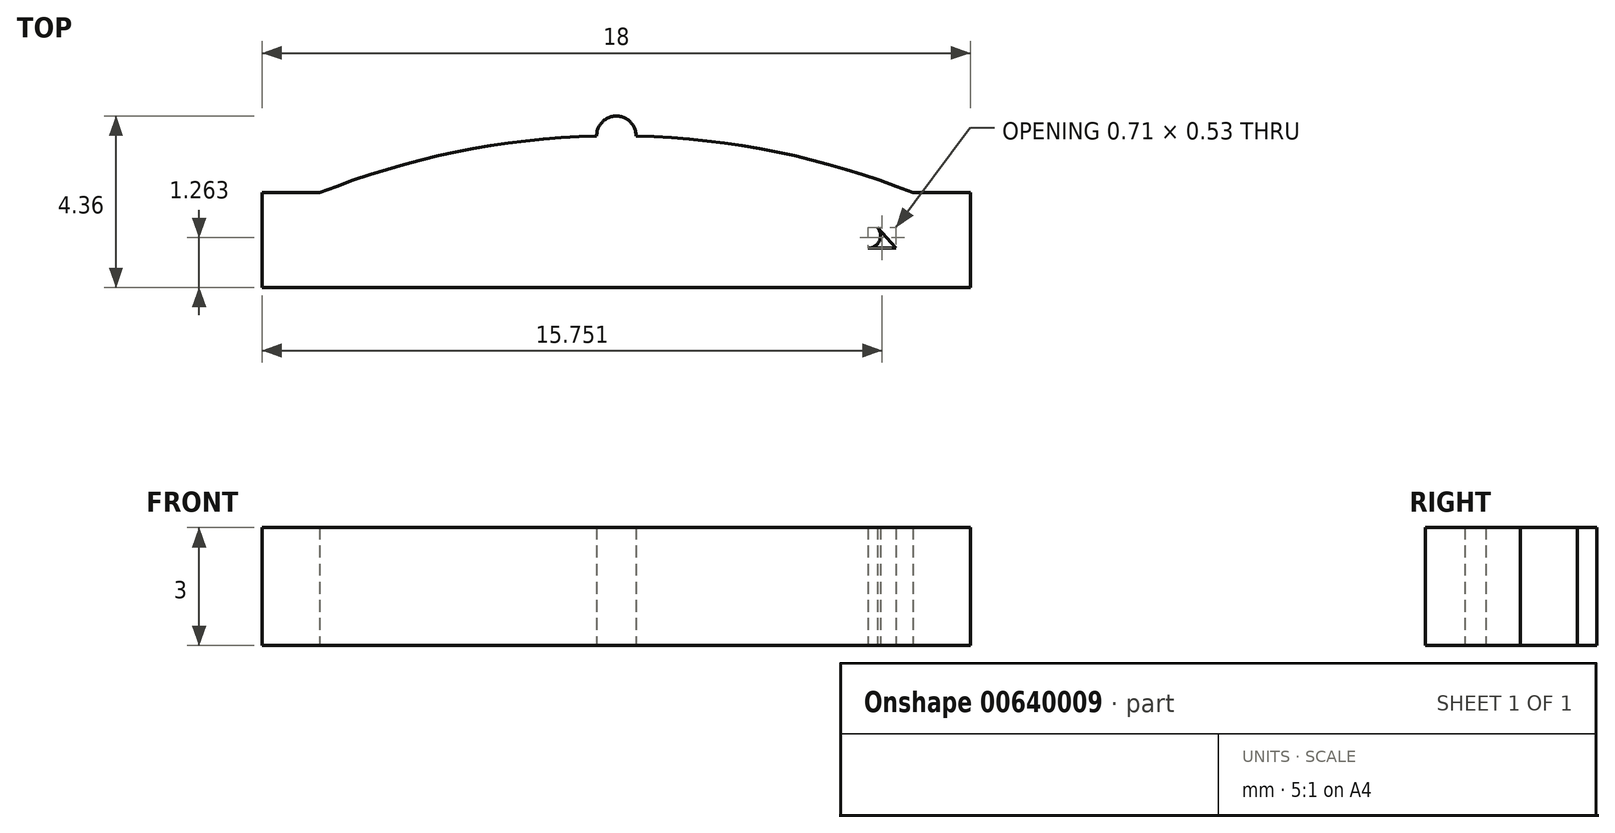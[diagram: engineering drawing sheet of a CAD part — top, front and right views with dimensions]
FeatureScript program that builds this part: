
annotation { "Feature Type Name" : "Feature", "Feature Type Description" : "" }
export const myFeature = defineFeature(function(context is Context, id is Id, definition is map)
    precondition{}
    {
        {
            var Q0;
            Q0=qCreatedBy(makeId("Top.planeOp"),FACE);
            var sketch = newSketch(context, id + "F0", { "sketchPlane" : qUnion([Q0])});
            skLineSegment(sketch, "E0.bottom", {"start": v(9, -13.15) * mm, "end": v(-9, -13.15) * mm});
            skLineSegment(sketch, "E0.top", {"start": v(9, -12.15) * mm, "end": v(-9, -12.15) * mm});
            skLineSegment(sketch, "E0.left", {"start": v(9, -13.15) * mm, "end": v(9, -12.15) * mm});
            skLineSegment(sketch, "E0.right", {"start": v(-9, -13.15) * mm, "end": v(-9, -12.15) * mm});
            skPoint(sketch, "E0.middle", {"position": v(0, -12.65) * mm});
            skArc(sketch, "E1", {"start": v(0, -10.1) * mm, "mid": v(-3.87, -10.48) * mm, "end": v(-7.58, -11.63) * mm});
            skLineSegment(sketch, "E2", {"start": v(0, -10.1) * mm, "end": v(13.67, -10.1) * mm, "construction": true});
            skArc(sketch, "E3.0", {"start": v(0, -9.3) * mm, "mid": v(-3.84, -9.66) * mm, "end": v(-7.53, -10.74) * mm});
            skLineSegment(sketch, "E4", {"start": v(-7.6, -12.15) * mm, "end": v(-7.58, -11.63) * mm});
            skLineSegment(sketch, "E5", {"start": v(-9, -12.15) * mm, "end": v(-9, -10.74) * mm});
            skLineSegment(sketch, "E6", {"start": v(-9, -10.74) * mm, "end": v(-7.53, -10.74) * mm});
            skLineSegment(sketch, "E7", {"start": v(0, -10.1) * mm, "end": v(0, -5.16) * mm, "construction": true});
            skArc(sketch, "E8.MirrorCS", {"start": v(0, -9.3) * mm, "mid": v(3.84, -9.66) * mm, "end": v(7.53, -10.74) * mm});
            skArc(sketch, "E9.MirrorCS", {"start": v(0, -10.1) * mm, "mid": v(3.87, -10.48) * mm, "end": v(7.58, -11.63) * mm});
            skLineSegment(sketch, "E10.MirrorCS", {"start": v(7.6, -12.15) * mm, "end": v(7.58, -11.63) * mm});
            skLineSegment(sketch, "E11.MirrorCS", {"start": v(9, -12.15) * mm, "end": v(9, -10.74) * mm});
            skLineSegment(sketch, "E12.MirrorCS", {"start": v(9, -10.74) * mm, "end": v(7.53, -10.74) * mm});
            skCircle(sketch, "E13", {"center": v(0, -9.3) * mm, "radius": 0.5 * mm});
            skPoint(sketch, "E14", {"position": v(-6.16, -11.1) * mm});
            skLineSegment(sketch, "E15", {"start": v(-6.16, -11.1) * mm, "end": v(-7.1, -12.15) * mm});
            skArc(sketch, "E16", {"start": v(-6.63, -11.62) * mm, "mid": v(-6.69, -11.96) * mm, "end": v(-6.4, -12.15) * mm});
            skLineSegment(sketch, "E17.MirrorCS", {"start": v(6.16, -11.1) * mm, "end": v(7.1, -12.15) * mm});
            skArc(sketch, "E18.MirrorCS", {"start": v(6.63, -11.62) * mm, "mid": v(6.69, -11.96) * mm, "end": v(6.4, -12.15) * mm});
            skSolve(sketch);
        }
        {
            var Q0;
            Q0 = qSketchRegion(id + "F0", true);
            var Q1;
            {var subQ0=sQuery(id+"F0.wireOp",EDGE,"E4");Q1=makeQuery(id+"F0.imprint","IMPRINT",FACE,{"disambiguationData":[TD([[makeQuery(id+"F0.imprint","IMPRINT",EDGE,{"derivedFrom":subQ0}),-1.0]])]});}
            var Q2;
            {var subQ3=sQuery(id+"F0.wireOp",EDGE,"E16");Q2=makeQuery(id+"F0.imprint","IMPRINT",FACE,{"disambiguationData":[TD([[makeQuery(id+"F0.imprint","IMPRINT",EDGE,{"derivedFrom":subQ3}),-1.0]])]});}
            var Q3;
            {var subQ3=sQuery(id+"F0.wireOp",EDGE,"E18.MirrorCS");Q3=makeQuery(id+"F0.imprint","IMPRINT",FACE,{"disambiguationData":[TD([[makeQuery(id+"F0.imprint","IMPRINT",EDGE,{"derivedFrom":subQ3}),1.0]])]});}
            var Q4;
            {var subQ4=sQuery(id+"F0.wireOp",EDGE,"E10.MirrorCS");Q4=makeQuery(id+"F0.imprint","IMPRINT",FACE,{"disambiguationData":[TD([[makeQuery(id+"F0.imprint","IMPRINT",EDGE,{"derivedFrom":subQ4}),1.0]])]});}
            extrude(context, id + "F1", {"entities" : qUnion([Q0, Q1, Q2, Q3, Q4]), "depth" : 3 * mm, "offsetDistance" : 25 * mm});
        }
    });
